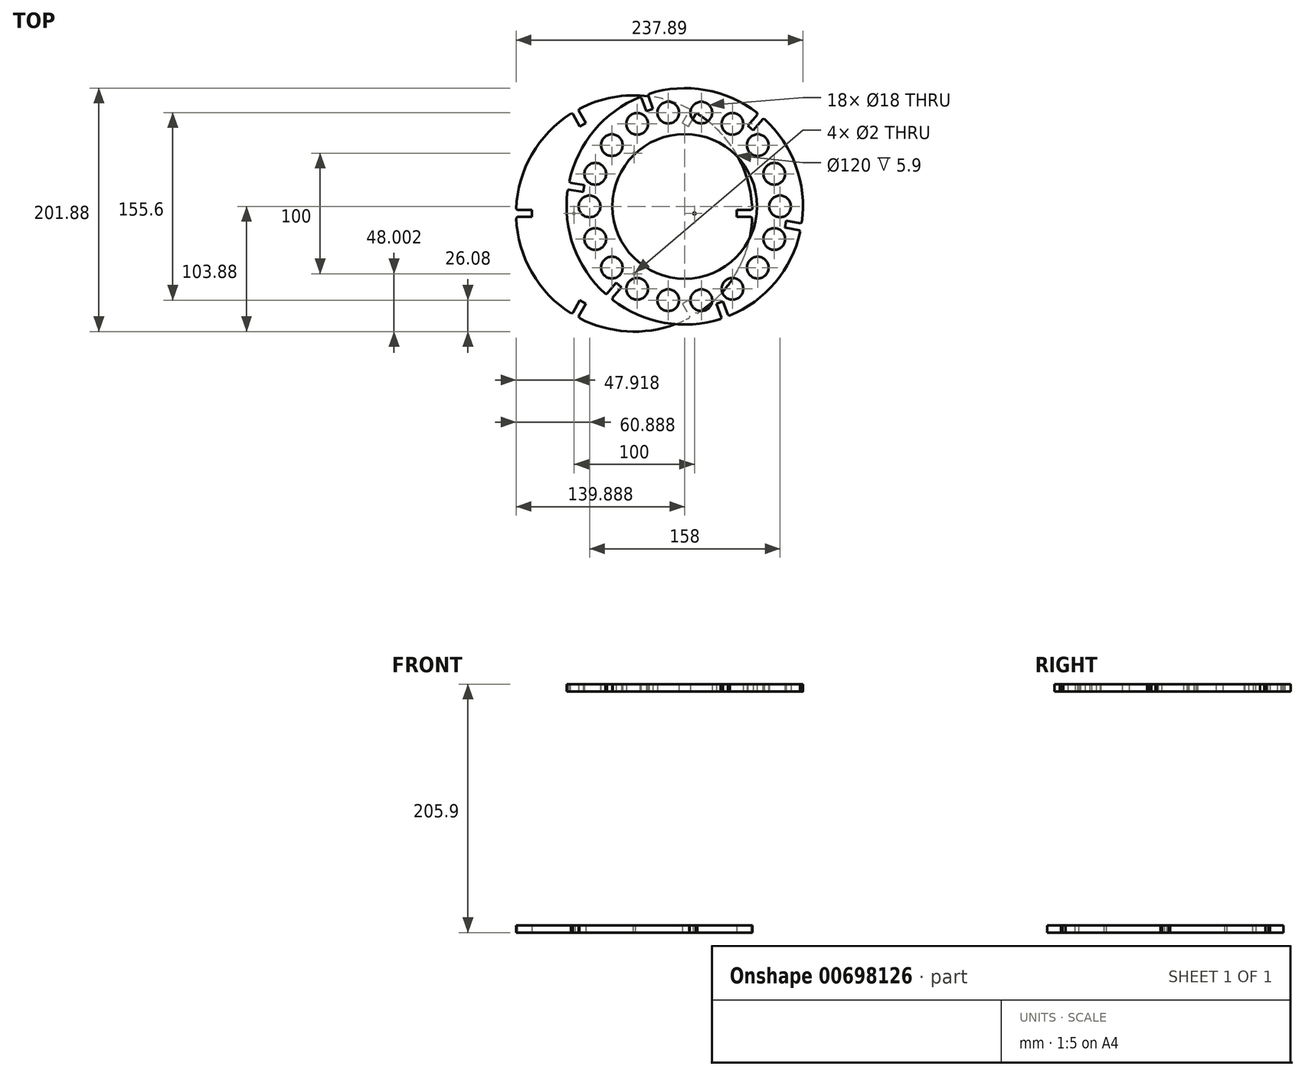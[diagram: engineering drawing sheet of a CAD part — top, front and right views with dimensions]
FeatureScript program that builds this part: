
annotation { "Feature Type Name" : "Feature", "Feature Type Description" : "" }
export const myFeature = defineFeature(function(context is Context, id is Id, definition is map)
    precondition{}
    {
        {
            assignVariable(context, id + "F0", {"name" : "wood", "anyValue" : 5.9 * mm});
        }
        {
            var Q0;
            Q0=qCreatedBy(makeId("Top.planeOp"),FACE);
            var sketch = newSketch(context, id + "F1", { "sketchPlane" : qUnion([Q0])});
            skCircle(sketch, "E0", {"center": v(-17.96, 0.58) * mm, "radius": 60 * mm});
            skArc(sketch, "E1", {"start": v(-114.93, 14.73) * mm, "mid": v(-110.05, -32.94) * mm, "end": v(-83.15, -72.6) * mm});
            skLineSegment(sketch, "E2", {"start": v(-77.96, 0.58) * mm, "end": v(-115.96, 0.58) * mm, "construction": true});
            skPoint(sketch, "E3", {"position": v(-96.96, 0.58) * mm});
            skCircle(sketch, "E4", {"center": v(-96.96, 0.58) * mm, "radius": 9 * mm});
            skPoint(sketch, "E5.1.0", {"position": v(-92.2, -26.44) * mm});
            skCircle(sketch, "E5.1.1", {"center": v(-92.2, -26.44) * mm, "radius": 9 * mm});
            skPoint(sketch, "E5.2.0", {"position": v(-78.48, -50.2) * mm});
            skCircle(sketch, "E5.2.1", {"center": v(-78.48, -50.2) * mm, "radius": 9 * mm});
            skPoint(sketch, "E5.3.0", {"position": v(-57.46, -67.84) * mm});
            skCircle(sketch, "E5.3.1", {"center": v(-57.46, -67.84) * mm, "radius": 9 * mm});
            skPoint(sketch, "E5.4.0", {"position": v(-31.68, -77.22) * mm});
            skCircle(sketch, "E5.4.1", {"center": v(-31.68, -77.22) * mm, "radius": 9 * mm});
            skPoint(sketch, "E5.5.0", {"position": v(-4.24, -77.22) * mm});
            skCircle(sketch, "E5.5.1", {"center": v(-4.24, -77.22) * mm, "radius": 9 * mm});
            skPoint(sketch, "E5.6.0", {"position": v(21.54, -67.84) * mm});
            skCircle(sketch, "E5.6.1", {"center": v(21.54, -67.84) * mm, "radius": 9 * mm});
            skPoint(sketch, "E5.7.0", {"position": v(42.56, -50.2) * mm});
            skCircle(sketch, "E5.7.1", {"center": v(42.56, -50.2) * mm, "radius": 9 * mm});
            skPoint(sketch, "E5.8.0", {"position": v(56.27, -26.44) * mm});
            skCircle(sketch, "E5.8.1", {"center": v(56.27, -26.44) * mm, "radius": 9 * mm});
            skPoint(sketch, "E5.9.0", {"position": v(61.04, 0.58) * mm});
            skCircle(sketch, "E5.9.1", {"center": v(61.04, 0.58) * mm, "radius": 9 * mm});
            skPoint(sketch, "E5.10.0", {"position": v(56.27, 27.6) * mm});
            skCircle(sketch, "E5.10.1", {"center": v(56.27, 27.6) * mm, "radius": 9 * mm});
            skPoint(sketch, "E5.11.0", {"position": v(42.56, 51.36) * mm});
            skCircle(sketch, "E5.11.1", {"center": v(42.56, 51.36) * mm, "radius": 9 * mm});
            skPoint(sketch, "E5.12.0", {"position": v(21.54, 69) * mm});
            skCircle(sketch, "E5.12.1", {"center": v(21.54, 69) * mm, "radius": 9 * mm});
            skPoint(sketch, "E5.13.0", {"position": v(-4.24, 78.38) * mm});
            skCircle(sketch, "E5.13.1", {"center": v(-4.24, 78.38) * mm, "radius": 9 * mm});
            skPoint(sketch, "E5.14.0", {"position": v(-31.68, 78.38) * mm});
            skCircle(sketch, "E5.14.1", {"center": v(-31.68, 78.38) * mm, "radius": 9 * mm});
            skPoint(sketch, "E5.15.0", {"position": v(-57.46, 69) * mm});
            skCircle(sketch, "E5.15.1", {"center": v(-57.46, 69) * mm, "radius": 9 * mm});
            skLineSegment(sketch, "E6", {"start": v(-129.15, 20.19) * mm, "end": v(-17.96, 0.58) * mm, "construction": true});
            skPoint(sketch, "E7", {"position": v(-114.47, 17.6) * mm});
            skLineSegment(sketch, "E8.bottom", {"start": v(-102.13, 12.48) * mm, "end": v(-114.93, 14.73) * mm});
            skLineSegment(sketch, "E8.top", {"start": v(-101.13, 18.19) * mm, "end": v(-113.93, 20.45) * mm});
            skLineSegment(sketch, "E8.left", {"start": v(-102.13, 12.48) * mm, "end": v(-101.13, 18.19) * mm});
            skPoint(sketch, "E9", {"position": v(-114.93, 14.73) * mm});
            skPoint(sketch, "E10.orphan", {"position": v(-126.81, 22.72) * mm});
            skPoint(sketch, "E8.right.start.orphan", {"position": v(-127.82, 17) * mm});
            skLineSegment(sketch, "E11.1.0", {"start": v(-70.35, -66.37) * mm, "end": v(-74.8, -62.64) * mm});
            skPoint(sketch, "E11.1.1", {"position": v(-80.96, -74.5) * mm});
            skLineSegment(sketch, "E11.1.2", {"start": v(-74.8, -62.64) * mm, "end": v(-83.15, -72.6) * mm});
            skPoint(sketch, "E11.1.3", {"position": v(-78.7, -76.32) * mm});
            skLineSegment(sketch, "E11.1.4", {"start": v(-70.35, -66.37) * mm, "end": v(-78.7, -76.32) * mm});
            skPoint(sketch, "E11.1.5", {"position": v(-80.96, -74.5) * mm});
            skLineSegment(sketch, "E11.2.0", {"start": v(13.82, -78.26) * mm, "end": v(8.37, -80.25) * mm});
            skPoint(sketch, "E11.2.1", {"position": v(15.56, -91.51) * mm});
            skLineSegment(sketch, "E11.2.2", {"start": v(8.37, -80.25) * mm, "end": v(12.82, -92.46) * mm});
            skPoint(sketch, "E11.2.3", {"position": v(18.27, -90.48) * mm});
            skLineSegment(sketch, "E11.2.4", {"start": v(13.82, -78.26) * mm, "end": v(18.27, -90.48) * mm});
            skPoint(sketch, "E11.2.5", {"position": v(15.56, -91.51) * mm});
            skLineSegment(sketch, "E11.3.0", {"start": v(66.2, -11.32) * mm, "end": v(65.2, -17.03) * mm});
            skPoint(sketch, "E11.3.1", {"position": v(78.55, -16.44) * mm});
            skLineSegment(sketch, "E11.3.2", {"start": v(65.2, -17.03) * mm, "end": v(78, -19.29) * mm});
            skPoint(sketch, "E11.3.3", {"position": v(79.01, -13.57) * mm});
            skLineSegment(sketch, "E11.3.4", {"start": v(66.2, -11.32) * mm, "end": v(79.01, -13.57) * mm});
            skPoint(sketch, "E11.3.5", {"position": v(78.55, -16.44) * mm});
            skLineSegment(sketch, "E11.4.0", {"start": v(34.43, 67.52) * mm, "end": v(38.87, 63.8) * mm});
            skPoint(sketch, "E11.4.1", {"position": v(45.03, 75.65) * mm});
            skLineSegment(sketch, "E11.4.2", {"start": v(38.87, 63.8) * mm, "end": v(47.22, 73.76) * mm});
            skPoint(sketch, "E11.4.3", {"position": v(42.78, 77.48) * mm});
            skLineSegment(sketch, "E11.4.4", {"start": v(34.43, 67.52) * mm, "end": v(42.78, 77.48) * mm});
            skPoint(sketch, "E11.4.5", {"position": v(45.03, 75.65) * mm});
            skLineSegment(sketch, "E11.5.0", {"start": v(-49.74, 79.42) * mm, "end": v(-44.3, 81.4) * mm});
            skPoint(sketch, "E11.5.1", {"position": v(-51.48, 92.67) * mm});
            skLineSegment(sketch, "E11.5.2", {"start": v(-44.3, 81.4) * mm, "end": v(-48.74, 93.62) * mm});
            skPoint(sketch, "E11.5.3", {"position": v(-54.2, 91.64) * mm});
            skLineSegment(sketch, "E11.5.4", {"start": v(-49.74, 79.42) * mm, "end": v(-54.2, 91.64) * mm});
            skPoint(sketch, "E11.5.5", {"position": v(-51.48, 92.67) * mm});
            skPoint(sketch, "E12.0.16.0", {"position": v(-78.48, 51.36) * mm});
            skCircle(sketch, "E12.1.16.0", {"center": v(-78.48, 51.36) * mm, "radius": 9 * mm});
            skPoint(sketch, "E12.0.17.0", {"position": v(-92.2, 27.6) * mm});
            skCircle(sketch, "E12.1.17.0", {"center": v(-92.2, 27.6) * mm, "radius": 9 * mm});
            skArc(sketch, "E13.trimOffspring", {"start": v(-54.2, 91.64) * mm, "mid": v(-93.03, 63.57) * mm, "end": v(-113.93, 20.45) * mm});
            skArc(sketch, "E14.trimOffspring", {"start": v(42.78, 77.48) * mm, "mid": v(-0.94, 97.1) * mm, "end": v(-48.74, 93.62) * mm});
            skArc(sketch, "E15.trimOffspring", {"start": v(79.01, -13.57) * mm, "mid": v(74.13, 34.1) * mm, "end": v(47.22, 73.76) * mm});
            skArc(sketch, "E16.trimOffspring", {"start": v(18.27, -90.48) * mm, "mid": v(57.11, -62.41) * mm, "end": v(78, -19.29) * mm});
            skArc(sketch, "E17.trimOffspring", {"start": v(-78.7, -76.32) * mm, "mid": v(-34.98, -95.93) * mm, "end": v(12.82, -92.46) * mm});
            skSolve(sketch);
        }
        {
            var Q0;
            Q0 = qSketchRegion(id + "F1", true);
            extrude(context, id + "F2", {"entities" : qUnion([Q0]), "depth" : getVariable(context, 'wood'), "offsetDistance" : 25 * mm});
        }
        {
            var Q0;
            Q0=qCreatedBy(makeId("Top.planeOp"),FACE);
            cPlane(context, id + "F3", {"entities" : qUnion([Q0]), "cplaneType" : CPlaneType.OFFSET, "offset" : 200 * mm, "oppositeDirection" : true, "width" : 150 * mm, "height" : 150 * mm});
        }
        {
            var Q0;
            Q0=qCreatedBy(id+"F3.planeOp",FACE);
            var sketch = newSketch(context, id + "F4", { "sketchPlane" : qUnion([Q0])});
            skArc(sketch, "E18", {"start": v(-157.89, -8.2) * mm, "mid": v(-144.8, -54.3) * mm, "end": v(-111.42, -88.68) * mm});
            skCircle(sketch, "E19", {"center": v(-59.93, -5.3) * mm, "radius": 60 * mm});
            skLineSegment(sketch, "E20", {"start": v(-59.93, -5.3) * mm, "end": v(-182.47, -5.3) * mm, "construction": true});
            skPoint(sketch, "E21", {"position": v(-157.93, -5.3) * mm});
            skLineSegment(sketch, "E22.bottom", {"start": v(-144.89, -8.2) * mm, "end": v(-157.89, -8.2) * mm});
            skLineSegment(sketch, "E22.top", {"start": v(-144.89, -2.4) * mm, "end": v(-157.89, -2.4) * mm});
            skLineSegment(sketch, "E22.left", {"start": v(-144.89, -8.2) * mm, "end": v(-144.89, -2.4) * mm});
            skPoint(sketch, "E23", {"position": v(-157.89, -2.4) * mm});
            skPoint(sketch, "E24", {"position": v(-157.89, -8.2) * mm});
            skPoint(sketch, "E25.orphan", {"position": v(-170.98, -2.4) * mm});
            skPoint(sketch, "E26.orphan", {"position": v(-170.98, -8.2) * mm});
            skPoint(sketch, "E27.1.0", {"position": v(-111.42, -88.68) * mm});
            skPoint(sketch, "E27.1.1", {"position": v(-106.4, -91.58) * mm});
            skPoint(sketch, "E27.1.2", {"position": v(-108.93, -90.17) * mm});
            skLineSegment(sketch, "E27.1.3", {"start": v(-99.9, -80.32) * mm, "end": v(-106.4, -91.58) * mm});
            skLineSegment(sketch, "E27.1.4", {"start": v(-104.92, -77.42) * mm, "end": v(-111.42, -88.68) * mm});
            skLineSegment(sketch, "E27.1.5", {"start": v(-99.9, -80.32) * mm, "end": v(-104.92, -77.42) * mm});
            skPoint(sketch, "E27.1.6", {"position": v(-108.93, -90.17) * mm});
            skPoint(sketch, "E27.2.0", {"position": v(-13.47, -91.58) * mm});
            skPoint(sketch, "E27.2.1", {"position": v(-8.44, -88.68) * mm});
            skPoint(sketch, "E27.2.2", {"position": v(-10.93, -90.17) * mm});
            skLineSegment(sketch, "E27.2.3", {"start": v(-14.94, -77.42) * mm, "end": v(-8.44, -88.68) * mm});
            skLineSegment(sketch, "E27.2.4", {"start": v(-19.97, -80.32) * mm, "end": v(-13.47, -91.58) * mm});
            skLineSegment(sketch, "E27.2.5", {"start": v(-14.94, -77.42) * mm, "end": v(-19.97, -80.32) * mm});
            skPoint(sketch, "E27.2.6", {"position": v(-10.93, -90.17) * mm});
            skPoint(sketch, "E27.3.0", {"position": v(38.02, -8.2) * mm});
            skPoint(sketch, "E27.3.1", {"position": v(38.02, -2.4) * mm});
            skPoint(sketch, "E27.3.2", {"position": v(38.07, -5.3) * mm});
            skLineSegment(sketch, "E27.3.3", {"start": v(25.02, -2.4) * mm, "end": v(38.02, -2.4) * mm});
            skLineSegment(sketch, "E27.3.4", {"start": v(25.02, -8.2) * mm, "end": v(38.02, -8.2) * mm});
            skLineSegment(sketch, "E27.3.5", {"start": v(25.02, -2.4) * mm, "end": v(25.02, -8.2) * mm});
            skPoint(sketch, "E27.3.6", {"position": v(38.07, -5.3) * mm});
            skPoint(sketch, "E27.4.0", {"position": v(-8.44, 78.09) * mm});
            skPoint(sketch, "E27.4.1", {"position": v(-13.47, 80.99) * mm});
            skPoint(sketch, "E27.4.2", {"position": v(-10.93, 79.57) * mm});
            skLineSegment(sketch, "E27.4.3", {"start": v(-19.97, 69.73) * mm, "end": v(-13.47, 80.99) * mm});
            skLineSegment(sketch, "E27.4.4", {"start": v(-14.94, 66.83) * mm, "end": v(-8.44, 78.09) * mm});
            skLineSegment(sketch, "E27.4.5", {"start": v(-19.97, 69.73) * mm, "end": v(-14.94, 66.83) * mm});
            skPoint(sketch, "E27.4.6", {"position": v(-10.93, 79.57) * mm});
            skPoint(sketch, "E27.5.0", {"position": v(-106.4, 80.99) * mm});
            skPoint(sketch, "E27.5.1", {"position": v(-111.42, 78.09) * mm});
            skPoint(sketch, "E27.5.2", {"position": v(-108.93, 79.57) * mm});
            skLineSegment(sketch, "E27.5.3", {"start": v(-104.92, 66.83) * mm, "end": v(-111.42, 78.09) * mm});
            skLineSegment(sketch, "E27.5.4", {"start": v(-99.9, 69.73) * mm, "end": v(-106.4, 80.99) * mm});
            skLineSegment(sketch, "E27.5.5", {"start": v(-104.92, 66.83) * mm, "end": v(-99.9, 69.73) * mm});
            skPoint(sketch, "E27.5.6", {"position": v(-108.93, 79.57) * mm});
            skArc(sketch, "E28.trimOffspring", {"start": v(-111.42, 78.09) * mm, "mid": v(-144.8, 43.7) * mm, "end": v(-157.89, -2.4) * mm});
            skArc(sketch, "E29.trimOffspring", {"start": v(-13.47, 80.99) * mm, "mid": v(-59.93, 92.7) * mm, "end": v(-106.4, 80.99) * mm});
            skArc(sketch, "E30.trimOffspring", {"start": v(38.02, -2.4) * mm, "mid": v(24.94, 43.7) * mm, "end": v(-8.44, 78.09) * mm});
            skArc(sketch, "E31.trimOffspring", {"start": v(-8.44, -88.68) * mm, "mid": v(24.94, -54.3) * mm, "end": v(38.02, -8.2) * mm});
            skArc(sketch, "E32.trimOffspring", {"start": v(-106.4, -91.58) * mm, "mid": v(-59.93, -103.3) * mm, "end": v(-13.47, -91.58) * mm});
            skPoint(sketch, "E33", {"position": v(-109.93, -5.3) * mm});
            skPoint(sketch, "E34.1.0", {"position": v(-59.93, -55.3) * mm});
            skPoint(sketch, "E34.2.0", {"position": v(-9.93, -5.3) * mm});
            skPoint(sketch, "E34.3.0", {"position": v(-59.93, 44.7) * mm});
            skSolve(sketch);
        }
        {
            var Q0;
            Q0 = qSketchRegion(id + "F4", true);
            var Q1;
            Q1=makeQuery(id+"F4.imprint","IMPRINT",FACE,{"disambiguationData":[TD([[makeQuery(id+"F4.imprint","IMPRINT",EDGE,{"derivedFrom":sQuery(id+"F4.wireOp",EDGE,"E19")}),1.0]])]});
            extrude(context, id + "F5", {"entities" : qUnion([Q0, Q1]), "depth" : getVariable(context, 'wood'), "offsetDistance" : 25 * mm});
        }
        {
            var Q0;
            Q0=makeQuery(id+"F2.opExtrude","SWEPT_EDGE",EDGE,{"disambiguationData":[OSD([sQuery(id+"F1.wireOp",EDGE,"E1"),sQuery(id+"F1.wireOp",EDGE,"E11.1.2")])]});
            var Q1;
            Q1=makeQuery(id+"F2.opExtrude","SWEPT_EDGE",EDGE,{"disambiguationData":[OSD([sQuery(id+"F1.wireOp",EDGE,"E11.1.4"),sQuery(id+"F1.wireOp",EDGE,"E17.trimOffspring")])]});
            var Q2;
            Q2=makeQuery(id+"F2.opExtrude","SWEPT_EDGE",EDGE,{"disambiguationData":[OSD([sQuery(id+"F1.wireOp",EDGE,"E11.2.2"),sQuery(id+"F1.wireOp",EDGE,"E17.trimOffspring")])]});
            var Q3;
            Q3=makeQuery(id+"F2.opExtrude","SWEPT_EDGE",EDGE,{"disambiguationData":[OSD([sQuery(id+"F1.wireOp",EDGE,"E11.2.4"),sQuery(id+"F1.wireOp",EDGE,"E16.trimOffspring")])]});
            var Q4;
            Q4=makeQuery(id+"F2.opExtrude","SWEPT_EDGE",EDGE,{"disambiguationData":[OSD([sQuery(id+"F1.wireOp",EDGE,"E11.3.2"),sQuery(id+"F1.wireOp",EDGE,"E16.trimOffspring")])]});
            var Q5;
            Q5=makeQuery(id+"F2.opExtrude","SWEPT_EDGE",EDGE,{"disambiguationData":[OSD([sQuery(id+"F1.wireOp",EDGE,"E11.3.4"),sQuery(id+"F1.wireOp",EDGE,"E15.trimOffspring")])]});
            var Q6;
            Q6=makeQuery(id+"F2.opExtrude","SWEPT_EDGE",EDGE,{"disambiguationData":[OSD([sQuery(id+"F1.wireOp",EDGE,"E11.4.2"),sQuery(id+"F1.wireOp",EDGE,"E15.trimOffspring")])]});
            var Q7;
            Q7=makeQuery(id+"F2.opExtrude","SWEPT_EDGE",EDGE,{"disambiguationData":[OSD([sQuery(id+"F1.wireOp",EDGE,"E11.4.4"),sQuery(id+"F1.wireOp",EDGE,"E14.trimOffspring")])]});
            var Q8;
            Q8=makeQuery(id+"F2.opExtrude","SWEPT_EDGE",EDGE,{"disambiguationData":[OSD([sQuery(id+"F1.wireOp",EDGE,"E11.5.2"),sQuery(id+"F1.wireOp",EDGE,"E14.trimOffspring")])]});
            var Q9;
            Q9=makeQuery(id+"F2.opExtrude","SWEPT_EDGE",EDGE,{"disambiguationData":[OSD([sQuery(id+"F1.wireOp",EDGE,"E11.5.4"),sQuery(id+"F1.wireOp",EDGE,"E13.trimOffspring")])]});
            var Q10;
            Q10=makeQuery(id+"F2.opExtrude","SWEPT_EDGE",EDGE,{"disambiguationData":[OSD([sQuery(id+"F1.wireOp",EDGE,"E8.top"),sQuery(id+"F1.wireOp",EDGE,"E13.trimOffspring")])]});
            var Q11;
            Q11=makeQuery(id+"F2.opExtrude","SWEPT_EDGE",EDGE,{"disambiguationData":[OSD([sQuery(id+"F1.wireOp",EDGE,"E1"),sQuery(id+"F1.wireOp",EDGE,"E8.bottom")])]});
            var Q12;
            Q12=makeQuery(id+"F5.opExtrude","SWEPT_EDGE",EDGE,{"disambiguationData":[OSD([sQuery(id+"F4.wireOp",EDGE,"E18"),sQuery(id+"F4.wireOp",EDGE,"E27.1.4")])]});
            var Q13;
            Q13=makeQuery(id+"F5.opExtrude","SWEPT_EDGE",EDGE,{"disambiguationData":[OSD([sQuery(id+"F4.wireOp",EDGE,"E27.1.3"),sQuery(id+"F4.wireOp",EDGE,"E32.trimOffspring")])]});
            var Q14;
            Q14=makeQuery(id+"F5.opExtrude","SWEPT_EDGE",EDGE,{"disambiguationData":[OSD([sQuery(id+"F4.wireOp",EDGE,"E27.2.4"),sQuery(id+"F4.wireOp",EDGE,"E32.trimOffspring")])]});
            var Q15;
            Q15=makeQuery(id+"F5.opExtrude","SWEPT_EDGE",EDGE,{"disambiguationData":[OSD([sQuery(id+"F4.wireOp",EDGE,"E27.2.3"),sQuery(id+"F4.wireOp",EDGE,"E31.trimOffspring")])]});
            var Q16;
            Q16=makeQuery(id+"F5.opExtrude","SWEPT_EDGE",EDGE,{"disambiguationData":[OSD([sQuery(id+"F4.wireOp",EDGE,"E27.3.4"),sQuery(id+"F4.wireOp",EDGE,"E31.trimOffspring")])]});
            var Q17;
            Q17=makeQuery(id+"F5.opExtrude","SWEPT_EDGE",EDGE,{"disambiguationData":[OSD([sQuery(id+"F4.wireOp",EDGE,"E27.3.3"),sQuery(id+"F4.wireOp",EDGE,"E30.trimOffspring")])]});
            var Q18;
            Q18=makeQuery(id+"F5.opExtrude","SWEPT_EDGE",EDGE,{"disambiguationData":[OSD([sQuery(id+"F4.wireOp",EDGE,"E27.4.4"),sQuery(id+"F4.wireOp",EDGE,"E30.trimOffspring")])]});
            var Q19;
            Q19=makeQuery(id+"F5.opExtrude","SWEPT_EDGE",EDGE,{"disambiguationData":[OSD([sQuery(id+"F4.wireOp",EDGE,"E27.4.3"),sQuery(id+"F4.wireOp",EDGE,"E29.trimOffspring")])]});
            var Q20;
            Q20=makeQuery(id+"F5.opExtrude","SWEPT_EDGE",EDGE,{"disambiguationData":[OSD([sQuery(id+"F4.wireOp",EDGE,"E27.5.4"),sQuery(id+"F4.wireOp",EDGE,"E29.trimOffspring")])]});
            var Q21;
            Q21=makeQuery(id+"F5.opExtrude","SWEPT_EDGE",EDGE,{"disambiguationData":[OSD([sQuery(id+"F4.wireOp",EDGE,"E27.5.3"),sQuery(id+"F4.wireOp",EDGE,"E28.trimOffspring")])]});
            var Q22;
            Q22=makeQuery(id+"F5.opExtrude","SWEPT_EDGE",EDGE,{"disambiguationData":[OSD([sQuery(id+"F4.wireOp",EDGE,"E22.top"),sQuery(id+"F4.wireOp",EDGE,"E28.trimOffspring")])]});
            var Q23;
            Q23=makeQuery(id+"F5.opExtrude","SWEPT_EDGE",EDGE,{"disambiguationData":[OSD([sQuery(id+"F4.wireOp",EDGE,"E18"),sQuery(id+"F4.wireOp",EDGE,"E22.bottom")])]});
            chamfer(context, id + "F6", {"entities" : qUnion([Q0, Q1, Q2, Q3, Q4, Q5, Q6, Q7, Q8, Q9, Q10, Q11, Q12, Q13, Q14, Q15, Q16, Q17, Q18, Q19, Q20, Q21, Q22, Q23]), "width" : 1 * mm, "tangentPropagation" : true});
        }
        {
            var Q0;
            Q0=sQuery(id+"F4.wireOp",VERTEX,"E33");
            var Q1;
            Q1=sQuery(id+"F4.wireOp",VERTEX,"E34.2.0");
            var Q2;
            Q2=sQuery(id+"F4.wireOp",VERTEX,"E34.3.0");
            var Q3;
            Q3=sQuery(id+"F4.wireOp",VERTEX,"E34.1.0");
            var Q4;
            Q4=makeQuery(id+"F5.opExtrude","SWEPT_BODY",BODY,{"disambiguationData":[OSD([sQuery(id+"F4.wireOp",EDGE,"E18"),sQuery(id+"F4.wireOp",EDGE,"E22.bottom"),sQuery(id+"F4.wireOp",EDGE,"E22.top"),sQuery(id+"F4.wireOp",EDGE,"E22.left"),sQuery(id+"F4.wireOp",EDGE,"E27.1.3"),sQuery(id+"F4.wireOp",EDGE,"E27.1.4"),sQuery(id+"F4.wireOp",EDGE,"E27.1.5"),sQuery(id+"F4.wireOp",EDGE,"E27.2.3"),sQuery(id+"F4.wireOp",EDGE,"E27.2.4"),sQuery(id+"F4.wireOp",EDGE,"E27.2.5"),sQuery(id+"F4.wireOp",EDGE,"E27.3.3"),sQuery(id+"F4.wireOp",EDGE,"E27.3.4"),sQuery(id+"F4.wireOp",EDGE,"E27.3.5"),sQuery(id+"F4.wireOp",EDGE,"E27.4.3"),sQuery(id+"F4.wireOp",EDGE,"E27.4.4"),sQuery(id+"F4.wireOp",EDGE,"E27.4.5"),sQuery(id+"F4.wireOp",EDGE,"E27.5.3"),sQuery(id+"F4.wireOp",EDGE,"E27.5.4"),sQuery(id+"F4.wireOp",EDGE,"E27.5.5"),sQuery(id+"F4.wireOp",EDGE,"E28.trimOffspring"),sQuery(id+"F4.wireOp",EDGE,"E29.trimOffspring"),sQuery(id+"F4.wireOp",EDGE,"E30.trimOffspring"),sQuery(id+"F4.wireOp",EDGE,"E31.trimOffspring"),sQuery(id+"F4.wireOp",EDGE,"E32.trimOffspring")])]});
            hole(context, id + "F7", {"style" : HoleStyle.SIMPLE, "endStyle" : HoleEndStyle.BLIND, "oppositeDirection" : true, "holeDiameter" : 2 * mm, "majorDiameter" : 5 * mm, "holeDepth" : 20 * mm, "isTappedThrough" : true, "tappedDepth" : 12 * mm, "tapClearance" : 3, "startFromSketch" : true, "locations" : qUnion([Q0, Q1, Q2, Q3]), "scope" : qUnion([Q4])});
        }
    });
